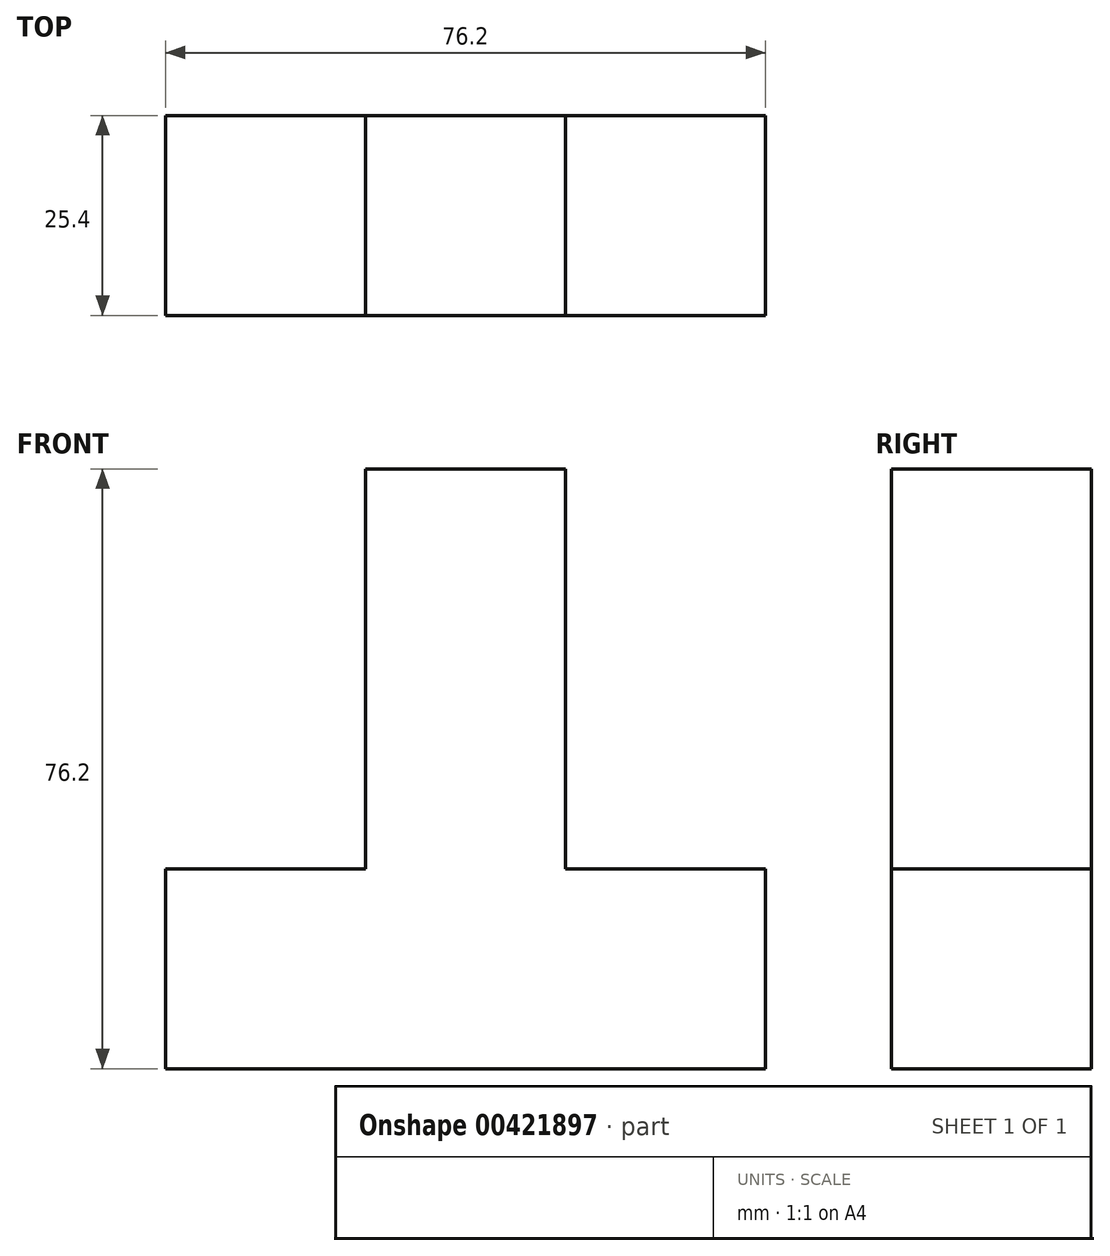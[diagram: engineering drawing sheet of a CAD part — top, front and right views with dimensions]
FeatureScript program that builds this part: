
annotation { "Feature Type Name" : "Feature", "Feature Type Description" : "" }
export const myFeature = defineFeature(function(context is Context, id is Id, definition is map)
    precondition{}
    {
        {
            var Q0;
            Q0=qCreatedBy(makeId("Front.planeOp"),FACE);
            var sketch = newSketch(context, id + "F0", { "sketchPlane" : qUnion([Q0])});
            skLineSegment(sketch, "E0", {"start": v(37.87, 0) * mm, "end": v(-38.33, 0) * mm});
            skLineSegment(sketch, "E1", {"start": v(-38.33, 0) * mm, "end": v(-38.33, 25.4) * mm});
            skLineSegment(sketch, "E2", {"start": v(-38.33, 25.4) * mm, "end": v(-12.93, 25.4) * mm});
            skLineSegment(sketch, "E3", {"start": v(-12.93, 25.4) * mm, "end": v(-12.93, 76.2) * mm});
            skLineSegment(sketch, "E4", {"start": v(-12.93, 76.2) * mm, "end": v(12.47, 76.2) * mm});
            skLineSegment(sketch, "E5", {"start": v(12.47, 76.2) * mm, "end": v(12.47, 25.4) * mm});
            skLineSegment(sketch, "E6", {"start": v(12.47, 25.4) * mm, "end": v(37.87, 25.4) * mm});
            skLineSegment(sketch, "E7", {"start": v(37.87, 25.4) * mm, "end": v(37.87, 0) * mm});
            skSolve(sketch);
        }
        {
            var Q0;
            Q0=makeQuery(id+"F0.imprint","IMPRINT",FACE,{"disambiguationData":[TD([[makeQuery(id+"F0.imprint","IMPRINT",EDGE,{"derivedFrom":sQuery(id+"F0.wireOp",EDGE,"E0")}),-1.0]])]});
            extrude(context, id + "F1", {"entities" : qUnion([Q0]), "depth" : 25.4 * mm});
        }
    });
